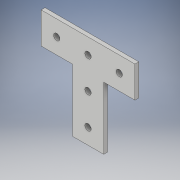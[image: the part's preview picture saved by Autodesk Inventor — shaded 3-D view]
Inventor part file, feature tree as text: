
AUTODESK INVENTOR PART (.ipt)
format: ipt  version: 2018 (Build 220112000, 112)  size: 113,152 bytes
history: native  units: in
note: dims shown in document units (in); Inventor stores cm internally (conversion verified against a paired STEP export)
features: extrude x1, sketch x1
ambient origin geometry x8: Origin, YZ Plane, XZ Plane, XY Plane, X Axis, Y Axis, Z Axis, Center Point
bodies: Solid1 (feature_tree)
feature tree (2):
  extrude  "Extrusion1"  Depth=3.0in
  sketch  "Sketch1"  dims[d0=1.0in d1=3.0in d2=3.0in d3=1.0in d4=0.2031in d5=1.0in d6=1.0in d7=1.0in d8=1.0in d9=0.125in d10=0.0in]
